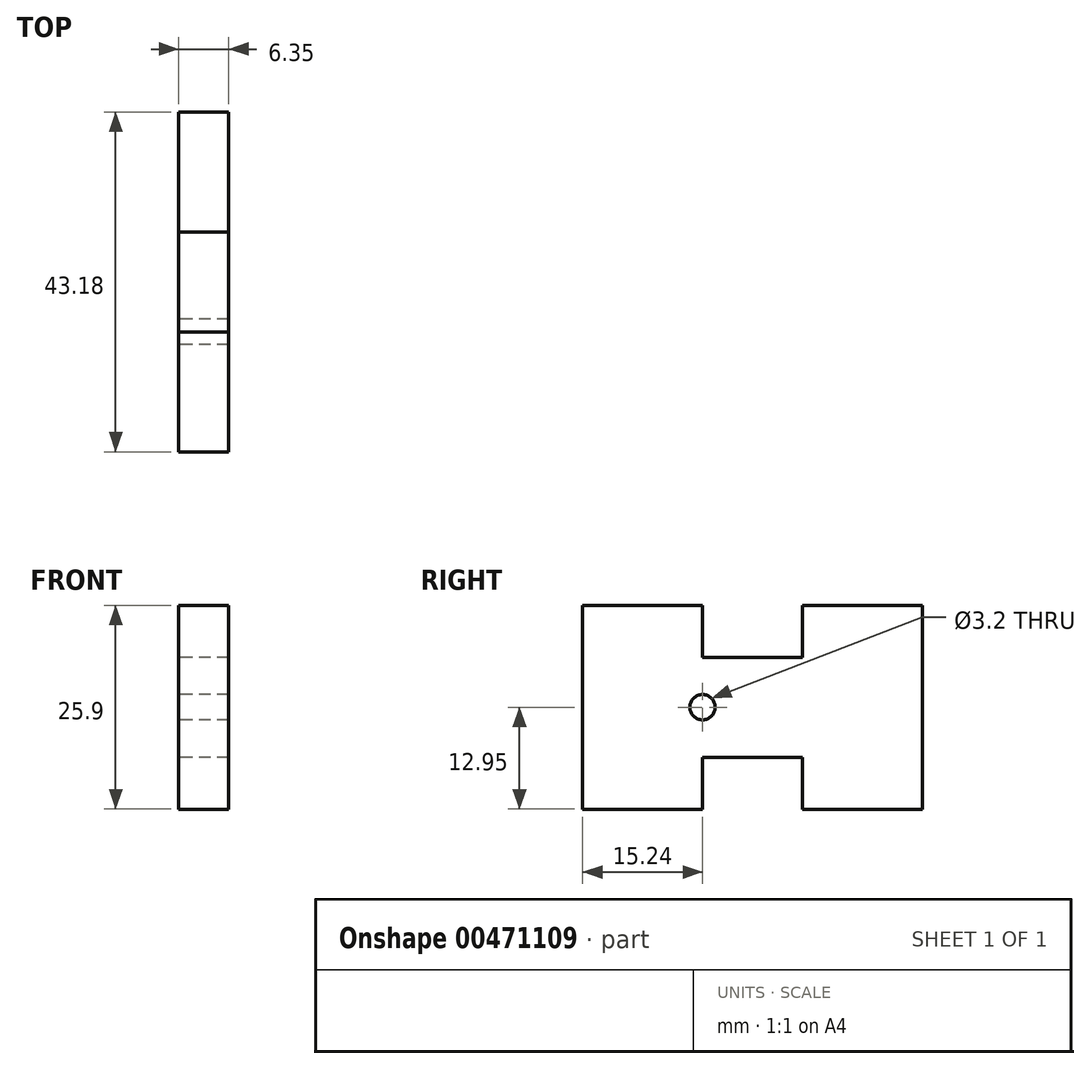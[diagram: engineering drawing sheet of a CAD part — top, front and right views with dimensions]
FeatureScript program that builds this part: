
annotation { "Feature Type Name" : "Feature", "Feature Type Description" : "" }
export const myFeature = defineFeature(function(context is Context, id is Id, definition is map)
    precondition{}
    {
        {
            var Q0;
            Q0=qCreatedBy(makeId("Right.planeOp"),FACE);
            var sketch = newSketch(context, id + "F0", { "sketchPlane" : qUnion([Q0])});
            skLineSegment(sketch, "E0", {"start": v(-6.35, 0) * mm, "end": v(-6.35, 6.6) * mm});
            skLineSegment(sketch, "E1", {"start": v(-6.35, 6.6) * mm, "end": v(-21.59, 6.6) * mm});
            skLineSegment(sketch, "E2.MirrorCS", {"start": v(6.35, 0) * mm, "end": v(6.35, 6.6) * mm});
            skLineSegment(sketch, "E3", {"start": v(-6.35, 0) * mm, "end": v(6.35, 0) * mm});
            skLineSegment(sketch, "E4", {"start": v(-21.59, 6.6) * mm, "end": v(-21.59, -19.3) * mm});
            skPoint(sketch, "E5.endSnap0", {"position": v(-21.59, -6.35) * mm});
            skLineSegment(sketch, "E6.MirrorCS", {"start": v(-6.35, -19.3) * mm, "end": v(-21.59, -19.3) * mm});
            skLineSegment(sketch, "E7.MirrorCS", {"start": v(-6.35, -12.7) * mm, "end": v(-6.35, -19.3) * mm});
            skLineSegment(sketch, "E8.MirrorCS", {"start": v(-6.35, -12.7) * mm, "end": v(6.35, -12.7) * mm});
            skLineSegment(sketch, "E9.MirrorCS", {"start": v(6.35, -12.7) * mm, "end": v(6.35, -19.3) * mm});
            skLineSegment(sketch, "E10.MirrorCS", {"start": v(6.35, -19.3) * mm, "end": v(21.59, -19.3) * mm});
            skLineSegment(sketch, "E11", {"start": v(21.59, -19.3) * mm, "end": v(21.59, 6.6) * mm});
            skLineSegment(sketch, "E12", {"start": v(6.35, 6.6) * mm, "end": v(21.59, 6.6) * mm});
            skCircle(sketch, "E13", {"center": v(-6.35, -6.35) * mm, "radius": 1.6 * mm});
            skSolve(sketch);
        }
        {
            var Q0;
            Q0=makeQuery(id+"F0.imprint","IMPRINT",FACE,{"disambiguationData":[TD([[makeQuery(id+"F0.imprint","IMPRINT",EDGE,{"derivedFrom":sQuery(id+"F0.wireOp",EDGE,"E0")}),1.0]])]});
            extrude(context, id + "F1", {"entities" : qUnion([Q0]), "depth" : 6.35 * mm});
        }
    });
